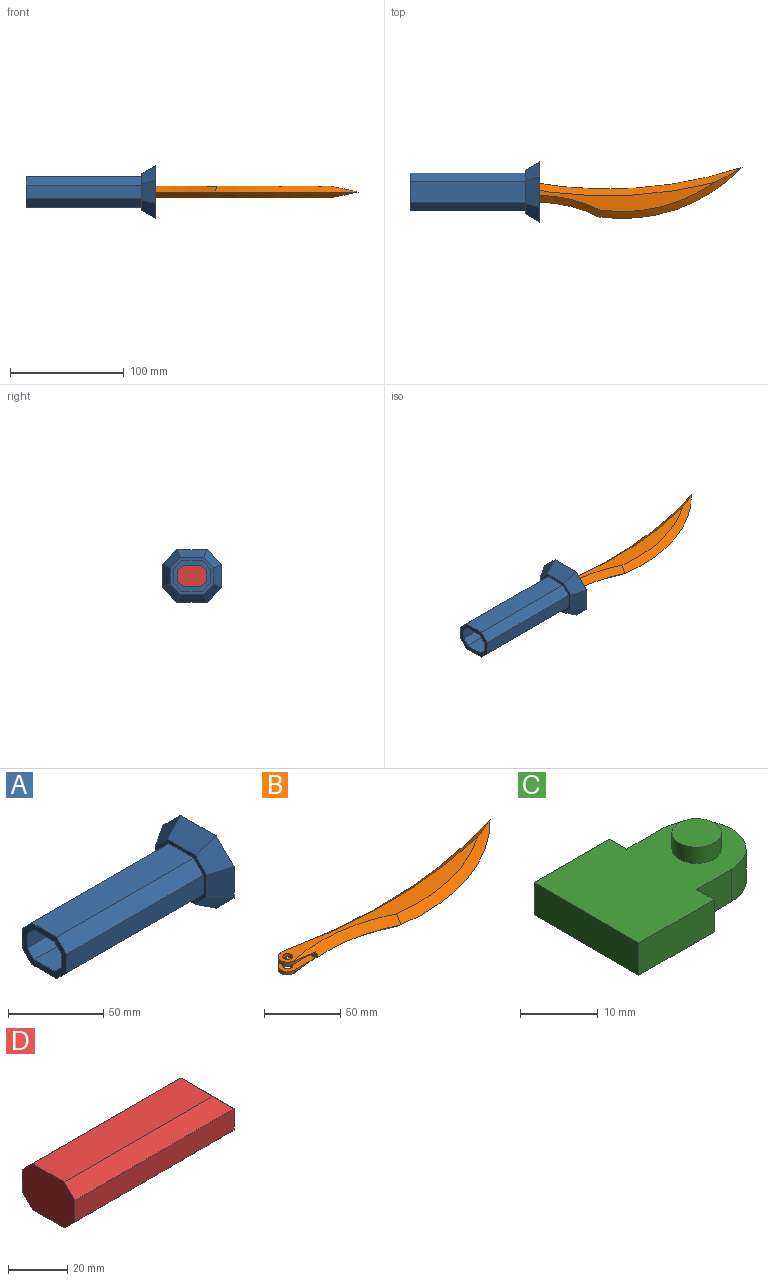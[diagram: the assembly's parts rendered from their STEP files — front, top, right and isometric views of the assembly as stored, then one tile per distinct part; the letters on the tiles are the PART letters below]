
ASSEMBLY  parts=4 mates=3
PART A: 27 faces, bbox 114.3x52.8x46.4 mm
  f0: plane 38.1x31.75mm, normal (-1,0,0), area 281.1mm2, adj f8,f9,f10,f11,f12,f13,f14,f15
  f1: plane 114.3x5.08mm, normal (0,-0.71,0.71), area 821.2mm2, adj f2,f16,f17,f26
  f2: plane 114.3x15.24mm, normal (0,0,1), area 1741.9mm2, adj f1,f3,f17,f26
  f3: plane 114.3x5.08mm, normal (0,0.71,0.71), area 821.2mm2, adj f2,f4,f17,f26
  f4: plane 114.3x8.89mm, normal (0,1,0), area 1016.1mm2, adj f3,f5,f17,f26
  f5: plane 114.3x5.08mm, normal (0,0.71,-0.71), area 821.2mm2, adj f4,f6,f17,f26
  f6: plane 114.3x15.24mm, normal (0,0,-1), area 1741.9mm2, adj f5,f7,f17,f26
  f7: plane 114.3x5.08mm, normal (0,-0.71,-0.71), area 821.2mm2, adj f6,f16,f17,f26
  f8: plane 20.23x12.7mm, normal (-0.5,-0.87,0), area 252.1mm2, adj f0,f9,f15,f17
  f9: plane 16.13x16.13mm, normal (-0.5,-0.61,-0.61), area 227mm2, adj f0,f8,f10,f17
  f10: plane 26.58x12.7mm, normal (-0.5,0,-0.87), area 345.2mm2, adj f0,f9,f11,f17
  f11: plane 16.13x16.13mm, normal (-0.5,0.61,-0.61), area 227mm2, adj f0,f10,f12,f17
  f12: plane 20.23x12.7mm, normal (-0.5,0.87,0), area 252.1mm2, adj f0,f11,f13,f17
  f13: plane 16.13x16.13mm, normal (-0.5,0.61,0.61), area 227mm2, adj f0,f12,f14,f17
  f14: plane 26.58x12.7mm, normal (-0.5,0,0.87), area 345.2mm2, adj f0,f13,f15,f17
  f15: plane 16.13x16.13mm, normal (-0.5,-0.61,0.61), area 227mm2, adj f0,f8,f14,f17
  f16: plane 114.3x8.89mm, normal (0,-1,0), area 1016.1mm2, adj f1,f7,f17,f26
  f17: plane 52.76x46.41mm, normal (1,0,0), area 1673.8mm2, adj f1,f2,f3,f4,f5,f6,f7,f8
  f18: plane 101.6x18.4mm, normal (0,0,-1), area 1869.1mm2, adj f0,f19,f25,f26
  f19: plane 101.6x7.31mm, normal (0,-0.71,-0.71), area 1050.6mm2, adj f0,f18,f20,f26
  f20: plane 101.6x12.05mm, normal (0,-1,0), area 1223.9mm2, adj f0,f19,f21,f26
  f21: plane 101.6x7.31mm, normal (0,-0.71,0.71), area 1050.6mm2, adj f0,f20,f22,f26
  f22: plane 101.6x18.4mm, normal (0,0,1), area 1869.1mm2, adj f0,f21,f23,f26
  f23: plane 101.6x7.31mm, normal (0,0.71,0.71), area 1050.6mm2, adj f0,f22,f24,f26
  f24: plane 101.6x12.05mm, normal (0,1,0), area 1223.9mm2, adj f0,f23,f25,f26
  f25: plane 101.6x7.31mm, normal (0,0.71,-0.71), area 1050.6mm2, adj f0,f18,f24,f26
  f26: plane 33.02x26.67mm, normal (-1,0,0), area 341.5mm2, adj f1,f2,f3,f4,f5,f6,f7,f16
PART B: 19 faces, bbox 216.9x49.1x10.2 mm
  f0: cylinder r=3.17mm len=6.35mm, axis (0,0,-1), area 50.7mm2, adj f7,f9
  f1: cone r=382.21mm half-angle=50deg, axis (0,0,1), area 1454.3mm2, adj f3,f4,f7,f8,f9,f11
  f2: cone r=122.5mm half-angle=50deg, axis (0,0,1), area 577.7mm2, adj f3,f5,f6,f7,f8,f9,f12
  f3: plane 18.45x5.08mm, normal (-1,0,0), area 78.2mm2, adj f1,f2,f9,f11,f12,f18
  f4: plane 18.06x2.54mm, normal (0,1,0), area 26.5mm2, adj f1,f5,f7,f9
  f5: cylinder r=6.35mm len=12.7mm, axis (0,0,-1), area 50.4mm2, adj f2,f4,f6,f7,f9
  f6: plane 17.12x2.18mm, normal (0,-1,0), area 15.8mm2, adj f2,f5,f9
  f7: plane 190x25.42mm, normal (0,0,1), area 1644.1mm2, adj f0,f1,f2,f4,f5,f8
  f8: cone r=140.13mm half-angle=50deg, axis (0,0,-1), area 963.6mm2, adj f1,f2,f7,f17
  f9: plane 25.5x12.7mm, normal (0,0,-1), area 274.6mm2, adj f0,f1,f2,f3,f4,f5,f6
  f10: cylinder r=3.17mm len=6.35mm, axis (0,0,1), area 50.7mm2, adj f16,f18
  f11: cone r=382.21mm half-angle=50deg, axis (0,0,-1), area 1454.3mm2, adj f1,f3,f13,f16,f17,f18
  f12: cone r=122.5mm half-angle=50deg, axis (0,0,-1), area 577.7mm2, adj f2,f3,f14,f15,f16,f17,f18
  f13: plane 18.06x2.54mm, normal (0,1,0), area 26.5mm2, adj f11,f14,f16,f18
  f14: cylinder r=6.35mm len=12.7mm, axis (0,0,1), area 50.4mm2, adj f12,f13,f15,f16,f18
  f15: plane 17.12x2.18mm, normal (0,-1,0), area 15.8mm2, adj f12,f14,f18
  f16: plane 190x25.42mm, normal (0,0,-1), area 1644.1mm2, adj f10,f11,f12,f13,f14,f17
  f17: cone r=140.13mm half-angle=50deg, axis (0,0,1), area 963.6mm2, adj f8,f11,f12,f16
  f18: plane 25.5x12.7mm, normal (0,0,1), area 274.6mm2, adj f3,f10,f11,f12,f13,f14,f15
PART C: 14 faces, bbox 26.4x19.1x10.2 mm
  f0: plane 6.35x5.08mm, normal (0,1,0), area 32.3mm2, adj f5,f6,f9,f13
  f1: cylinder r=3.17mm len=6.35mm, axis (0,0,-1), area 50.7mm2, adj f2,f6
  f2: plane 6.35x6.35mm, normal (0,0,1), area 31.7mm2, adj f1
  f3: plane 19.05x5.08mm, normal (-1,0,0), area 96.8mm2, adj f6,f8,f10,f13
  f4: plane 6.35x5.08mm, normal (0,-1,0), area 32.3mm2, adj f5,f6,f7,f13
  f5: cylinder r=6.35mm len=12.7mm, axis (0,0,-1), area 101.3mm2, adj f0,f4,f6,f13
  f6: plane 26.35x19.05mm, normal (0,0,1), area 372.4mm2, adj f0,f1,f3,f4,f5,f7,f8,f9
  f7: plane 5.08x3.18mm, normal (1,0,0), area 16.1mm2, adj f4,f6,f8,f13
  f8: plane 13.65x5.08mm, normal (0,-1,0), area 69.4mm2, adj f3,f6,f7,f13
  f9: plane 5.08x3.18mm, normal (1,0,0), area 16.1mm2, adj f0,f6,f10,f13
  f10: plane 13.65x5.08mm, normal (0,1,0), area 69.4mm2, adj f3,f6,f9,f13
  f11: cylinder r=3.17mm len=6.35mm, axis (0,0,1), area 50.7mm2, adj f12,f13
  f12: plane 6.35x6.35mm, normal (0,0,-1), area 31.7mm2, adj f11
  f13: plane 26.35x19.05mm, normal (0,0,-1), area 372.4mm2, adj f0,f3,f4,f5,f7,f8,f9,f10
PART D: 18 faces, bbox 76.2x25.4x19.1 mm
  f0: plane 8.89x3.18mm, normal (1,0,0), area 28.2mm2, adj f2,f6,f11,f16
  f1: plane 8.89x3.18mm, normal (1,0,0), area 28.2mm2, adj f4,f8,f11,f16
  f2: plane 76.2x8.89mm, normal (0,1,0), area 677.4mm2, adj f0,f3,f10,f15
  f3: plane 25.4x19.05mm, normal (-1,0,0), area 432.3mm2, adj f2,f4,f5,f10,f12,f13,f15,f17
  f4: plane 76.2x8.89mm, normal (0,-1,0), area 677.4mm2, adj f1,f3,f12,f17
  f5: plane 71.12x15.24mm, normal (0,0,1), area 1083.9mm2, adj f3,f10,f11,f12
  f6: plane 63.5x12.7mm, normal (0,-1,0), area 802.8mm2, adj f0,f7,f9,f11,f14,f16
  f7: plane 61.6x19.05mm, normal (0,0,-1), area 1173.4mm2, adj f6,f8,f9,f11
  f8: plane 63.5x12.7mm, normal (0,1,0), area 802.8mm2, adj f1,f7,f9,f11,f14,f16
  f9: plane 19.05x12.7mm, normal (1,0,0), area 241.9mm2, adj f6,f7,f8,f14
  f10: plane 76.2x5.08mm, normal (0,0.71,0.71), area 529.2mm2, adj f2,f3,f5,f11
  f11: plane 25.4x5.08mm, normal (0.71,0,0.71), area 94.7mm2, adj f0,f1,f5,f6,f7,f8,f10,f12
  f12: plane 76.2x5.08mm, normal (0,-0.71,0.71), area 529.2mm2, adj f3,f4,f5,f11
  f13: plane 71.12x15.24mm, normal (0,0,-1), area 1083.9mm2, adj f3,f15,f16,f17
  f14: plane 61.6x19.05mm, normal (0,0,1), area 1173.4mm2, adj f6,f8,f9,f16
  f15: plane 76.2x5.08mm, normal (0,0.71,-0.71), area 529.2mm2, adj f2,f3,f13,f16
  f16: plane 25.4x5.08mm, normal (0.71,0,-0.71), area 94.7mm2, adj f0,f1,f6,f8,f13,f14,f15,f17
  f17: plane 76.2x5.08mm, normal (0,-0.71,-0.71), area 529.2mm2, adj f3,f4,f13,f16
PLACE A t=(168,2.59,-9.11)mm
PLACE B t=(209.07,-33.25,29.67)mm
PLACE C t=(193.54,-52.4,29.67)mm
PLACE D rot(axis=(1,0,0),0deg) t=(213,-1.05,29.67)mm
MATE slider C.f3 <-> D.f0  axis (-1,0,0) through (129.9,-14.2,29.67)mm
MATE planar D.f4 <-> A.f4  axis (0,-1,0) through (180.7,-36.42,29.67)mm
MATE cylindrical B.f0 <-> C.f1  axis (0,0,1) through (149.9,-23.72,34.75)mm
